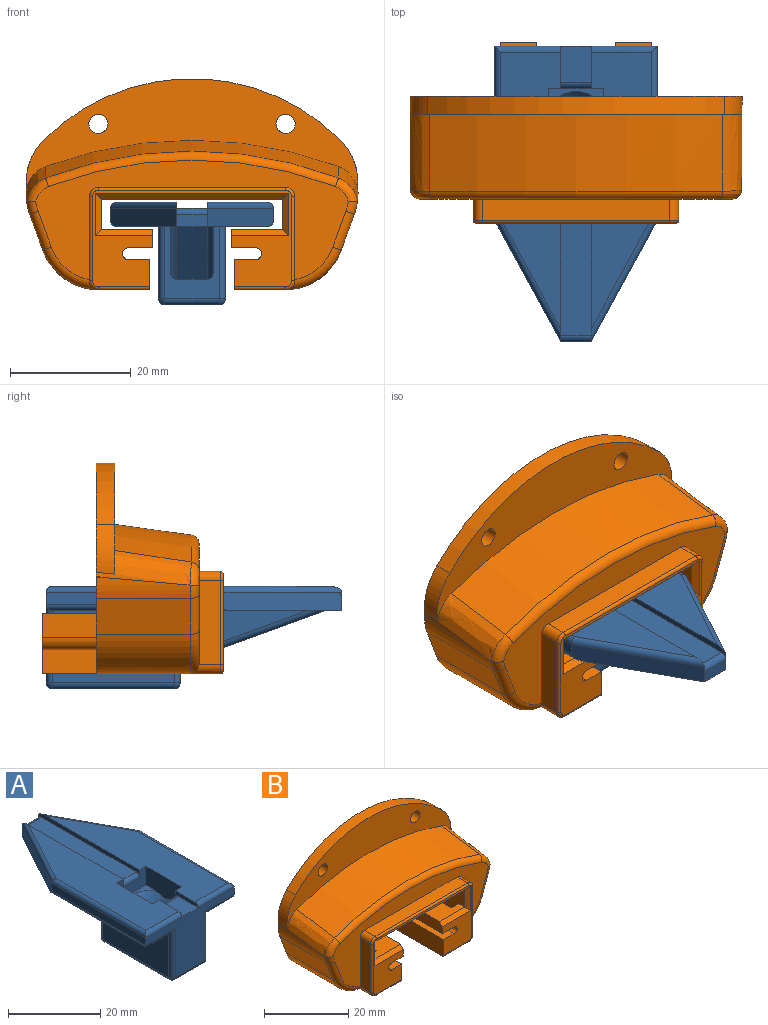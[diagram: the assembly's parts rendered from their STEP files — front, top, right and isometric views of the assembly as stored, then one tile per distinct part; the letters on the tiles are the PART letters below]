
ASSEMBLY  parts=2 mates=1
PART A: 58 faces, bbox 27.2x49.2x17.2 mm
  f0: plane 5x2mm, normal (0,1,0), area 10mm2, adj f2,f3,f15,f57
  f1: plane 20.2x12mm, normal (-1,0,0), area 242.4mm2, adj f15,f37,f43,f46
  f2: plane 20.2x11mm, normal (0.88,0.48,0), area 68.6mm2, adj f0,f9,f15,f16,f31,f49
  f3: plane 20.2x11mm, normal (-0.88,0.48,0), area 68.6mm2, adj f0,f13,f15,f17,f33,f52
  f4: plane 45.91x10mm, normal (0,0,1), area 345.3mm2, adj f12,f13,f19,f20,f22,f50,f51,f52
  f5: plane 45.91x10mm, normal (0,0,1), area 345.3mm2, adj f8,f9,f19,f20,f21,f47,f48,f49
  f6: plane 20.2x9mm, normal (0,0,-1), area 131.5mm2, adj f38,f39,f43,f44,f54
  f7: plane 9x3.32mm, normal (0,0,1), area 11.7mm2, adj f20,f21,f22,f25
  f8: plane 7x2mm, normal (-1,0,0), area 7mm2, adj f5,f10,f19,f47,f55
  f9: plane 31x2mm, normal (-1,0,0), area 31mm2, adj f2,f5,f11,f20,f49,f56,f57
  f10: plane 6x5mm, normal (0,0,1), area 30mm2, adj f8,f12,f18,f55
  f11: plane 29x5mm, normal (0,0,1), area 145mm2, adj f9,f13,f56,f57
  f12: plane 7x2mm, normal (1,0,0), area 7mm2, adj f4,f10,f19,f50,f55
  f13: plane 31x2mm, normal (1,0,0), area 31mm2, adj f3,f4,f11,f20,f52,f56,f57
  f14: plane 20.2x12mm, normal (1,0,0), area 242.4mm2, adj f15,f34,f39,f40
  f15: plane 48x25mm, normal (0,0,-1), area 616.6mm2, adj f0,f1,f2,f3,f14,f26,f27,f28
  f16: plane 28.8x2mm, normal (1,0,0), area 57.6mm2, adj f2,f18,f31,f48
  f17: plane 28.8x2mm, normal (-1,0,0), area 57.6mm2, adj f3,f18,f33,f51
  f18: plane 27x15mm, normal (0,-1,0), area 171mm2, adj f10,f16,f17,f32,f34,f35,f37,f38
  f19: plane 9x5mm, normal (0,1,0), area 35mm2, adj f4,f5,f8,f12,f21,f22,f23,f55
  f20: plane 9x5mm, normal (0,-1,0), area 35mm2, adj f4,f5,f7,f9,f13,f21,f22,f56
  f21: plane 11x5.51mm, normal (-1,0,0), area 56.4mm2, adj f5,f7,f19,f20,f23,f25
  f22: plane 11x5.5mm, normal (1,0,0), area 56.4mm2, adj f4,f7,f19,f20,f23,f25
  f23: plane 9x3.32mm, normal (0,0,1), area 11.7mm2, adj f19,f21,f22,f25
  f24: cylinder r=3mm len=9mm, axis (0,0,1), area 169.6mm2, adj f25,f54
  f25: cone r=3mm half-angle=45deg, axis (0,0,1), area 66.9mm2, adj f7,f21,f22,f23,f24
  f26: plane 12.15x9.15mm, normal (0,1,0), area 47.2mm2, adj f15,f27,f28,f29,f30,f40,f44,f46
  f27: plane 21.12x7.69mm, normal (1,0,0), area 81.1mm2, adj f15,f26,f53
  f28: plane 24.04x8.75mm, normal (0,0.34,-0.94), area 127.9mm2, adj f15,f26,f30,f53
  f29: plane 21.12x7.69mm, normal (-1,0,0), area 81.1mm2, adj f15,f26,f30
  f30: cylinder r=1mm len=24.38mm, axis (0,-0.94,-0.34), area 38.3mm2, adj f15,f26,f28,f29
  f31: cylinder r=1mm len=30.64mm, axis (0,1,0), area 45.7mm2, adj f2,f15,f16,f32
  f32: cylinder r=1mm len=9mm, axis (-1,0,0), area 12.6mm2, adj f15,f18,f31,f34
  f33: cylinder r=1mm len=30.64mm, axis (0,-1,0), area 45.7mm2, adj f3,f15,f17,f35
  f34: cylinder r=1mm len=13mm, axis (0,0,-1), area 19.4mm2, adj f14,f18,f32,f36
  f35: cylinder r=1mm len=9mm, axis (1,0,0), area 12.6mm2, adj f15,f18,f33,f37
  f36: sphere r=1mm, area 1.6mm2, adj f34,f38,f39
  f37: cylinder r=1mm len=13mm, axis (0,0,1), area 19.4mm2, adj f1,f18,f35,f41
  f38: cylinder r=1mm len=9mm, axis (-1,0,0), area 14.1mm2, adj f6,f18,f36,f41
  f39: cylinder r=1mm len=20.2mm, axis (0,1,0), area 31.7mm2, adj f6,f14,f36,f42
  f40: cylinder r=1mm len=12mm, axis (0,0,-1), area 18.8mm2, adj f14,f15,f26,f42
  f41: sphere r=1mm, area 1.6mm2, adj f37,f38,f43
  f42: sphere r=1mm, area 1.6mm2, adj f39,f40,f44
  f43: cylinder r=1mm len=20.2mm, axis (0,-1,0), area 31.7mm2, adj f1,f6,f41,f45
  f44: cylinder r=1mm len=9mm, axis (-1,0,0), area 14.1mm2, adj f6,f26,f42,f45
  f45: sphere r=1mm, area 1.6mm2, adj f43,f44,f46
  f46: cylinder r=1mm len=12mm, axis (0,0,-1), area 18.8mm2, adj f1,f15,f26,f45
  f47: cylinder r=1mm len=11mm, axis (1,0,0), area 16.7mm2, adj f5,f8,f18,f48
  f48: cylinder r=1mm len=28.8mm, axis (0,1,0), area 44.5mm2, adj f5,f16,f47,f49
  f49: cylinder r=1mm len=20.68mm, axis (0.48,-0.88,0), area 34.9mm2, adj f2,f5,f9,f48
  f50: cylinder r=1mm len=11mm, axis (1,0,0), area 16.7mm2, adj f4,f12,f18,f51
  f51: cylinder r=1mm len=28.8mm, axis (0,1,0), area 44.5mm2, adj f4,f17,f50,f52
  f52: cylinder r=1mm len=20.68mm, axis (-0.48,-0.88,0), area 34.9mm2, adj f3,f4,f13,f51
  f53: cylinder r=1mm len=24.38mm, axis (0,0.94,0.34), area 38.3mm2, adj f15,f26,f27,f28
  f54: torus R=4mm, axis (0,0,1), area 33.2mm2, adj f6,f24
  f55: cylinder r=1mm len=5mm, axis (-1,0,0), area 7.9mm2, adj f8,f10,f12,f19
  f56: cylinder r=1mm len=5mm, axis (1,0,0), area 7.9mm2, adj f9,f11,f13,f20
  f57: cylinder r=1mm len=5mm, axis (-1,0,0), area 7.9mm2, adj f0,f9,f11,f13
PART B: 137 faces, bbox 55.1x88.3x35.9 mm
  f0: plane 29x8.5mm, normal (0,0,1), area 179mm2, adj f30,f36,f41,f53,f123,f135
  f1: plane 9.5x9.04mm, normal (0,1,0), area 53.1mm2, adj f6,f11,f12,f28,f71,f90,f104
  f2: plane 55.01x35.01mm, normal (0,1,0), area 376.1mm2, adj f5,f8,f11,f21,f22,f24,f25,f26
  f3: plane 35x10mm, normal (0,1,0), area 125mm2, adj f6,f12,f14,f28,f29,f30,f79,f82
  f4: plane 0.84x0.5mm, normal (0,0,-1), area 0.4mm2, adj f8,f10,f74,f135
  f5: cylinder r=3.5mm len=18.5mm, axis (0,-1,0), area 41.8mm2, adj f2,f7,f52,f71,f83,f136
  f6: plane 14.5x2.5mm, normal (0,0,-1), area 36.2mm2, adj f1,f3,f12,f28
  f7: plane 0.84x0.5mm, normal (0,0,-1), area 0.4mm2, adj f5,f9,f83,f136
  f8: cylinder r=3.5mm len=18.5mm, axis (0,-1,0), area 41.8mm2, adj f2,f4,f53,f69,f74,f135
  f9: plane 5x0.5mm, normal (-1,0,0), area 2.5mm2, adj f7,f71,f83,f136
  f10: plane 5x0.5mm, normal (1,0,0), area 2.5mm2, adj f4,f69,f74,f135
  f11: plane 14.5x5.96mm, normal (-0.94,0,0.34), area 77.1mm2, adj f1,f2,f19,f90,f91,f103,f104,f105
  f12: plane 14.5x10mm, normal (1,0,0), area 131mm2, adj f1,f3,f6,f14,f19,f103,f104,f105
  f13: plane 9.47x5.86mm, normal (0,1,0), area 31.5mm2, adj f14,f18,f78,f79,f88,f92,f98,f100
  f14: plane 35x14.5mm, normal (0,0,1), area 465.5mm2, adj f3,f12,f13,f15,f19,f70,f79,f85
  f15: plane 14x3.13mm, normal (0,1,0), area 36.1mm2, adj f14,f16,f96,f99
  f16: cone r=65.52mm half-angle=8deg, axis (0,1,0), area 199.6mm2, adj f15,f85,f96,f99
  f17: plane 9.5x9.04mm, normal (0,1,0), area 53.1mm2, adj f30,f69,f78,f79,f82,f89,f101
  f18: cone r=65.52mm half-angle=8deg, axis (0,1,0), area 116.4mm2, adj f13,f85,f92,f98
  f19: plane 9.47x5.86mm, normal (0,1,0), area 31.5mm2, adj f11,f12,f14,f20,f91,f93,f95,f103
  f20: cone r=65.52mm half-angle=8deg, axis (0,1,0), area 116.4mm2, adj f19,f85,f93,f95
  f21: plane 1.31x0.2mm, normal (-1,0,0), area 0.1mm2, adj f2,f63,f67
  f22: cylinder r=34.71mm len=49.17mm, axis (0,1,0), area 163.9mm2, adj f2,f60,f61,f62
  f23: plane 51.81x19.84mm, normal (0,-1,0), area 348mm2, adj f56,f57,f58,f107,f108,f110,f111,f112
  f24: plane 1.31x0.2mm, normal (1,0,0), area 0.1mm2, adj f2,f66,f68
  f25: plane 15.5x5.96mm, normal (-0.94,0,-0.34), area 98.3mm2, adj f2,f63,f64,f113
  f26: plane 15.5x5.96mm, normal (0.94,0,-0.34), area 98.3mm2, adj f2,f65,f66,f108
  f27: plane 29.5x8.32mm, normal (0,0,-1), area 179.6mm2, adj f2,f36,f45,f48,f64,f124
  f28: plane 20x12.5mm, normal (-1,0,0), area 162.5mm2, adj f1,f3,f6,f29,f40,f71,f120,f136
  f29: plane 30x20mm, normal (0,0,-1), area 600mm2, adj f3,f28,f30,f121
  f30: plane 20x12.5mm, normal (1,0,0), area 162.5mm2, adj f0,f3,f17,f29,f69,f82,f122,f135
  f31: plane 10x6mm, normal (0,1,0), area 29.1mm2, adj f34,f37,f38,f39,f40,f46,f47,f49
  f32: cylinder r=1.59mm len=3.18mm, axis (0,-1,0), area 29.9mm2, adj f2,f60
  f33: cylinder r=1.59mm len=3.18mm, axis (0,-1,0), area 29.9mm2, adj f2,f60
  f34: plane 29.5x8.32mm, normal (0,0,-1), area 179.6mm2, adj f2,f31,f46,f49,f65,f130
  f35: plane 33x16mm, normal (0,-1,0), area 169mm2, adj f37,f38,f39,f41,f42,f43,f44,f45
  f36: plane 10x6mm, normal (0,1,0), area 29.1mm2, adj f0,f27,f41,f42,f43,f44,f45,f48
  f37: cylinder r=1mm len=30mm, axis (0,-1,0), area 94.2mm2, adj f31,f35,f38,f47
  f38: plane 30x4mm, normal (0,0,-1), area 120mm2, adj f31,f35,f37,f39
  f39: plane 30x3mm, normal (-1,0,0), area 89.5mm2, adj f31,f35,f38,f40,f119
  f40: plane 29x8.5mm, normal (0,0,1), area 179mm2, adj f28,f31,f39,f52,f119,f136
  f41: plane 30x3mm, normal (1,0,0), area 89.5mm2, adj f0,f35,f36,f42,f123
  f42: plane 30x4mm, normal (0,0,-1), area 120mm2, adj f35,f36,f41,f43
  f43: cylinder r=1mm len=30mm, axis (0,-1,0), area 94.2mm2, adj f35,f36,f42,f44
  f44: plane 30x3.5mm, normal (0,0,1), area 105mm2, adj f35,f36,f43,f45
  f45: plane 30x5mm, normal (1,0,0), area 149.9mm2, adj f27,f35,f36,f44,f124
  f46: plane 30x5mm, normal (-1,0,0), area 149.9mm2, adj f31,f34,f35,f47,f130
  f47: plane 30x3.5mm, normal (0,0,1), area 105mm2, adj f31,f35,f37,f46
  f48: plane 9x4mm, normal (-1,0,0), area 36mm2, adj f2,f27,f36,f55
  f49: plane 9x4mm, normal (1,0,0), area 36mm2, adj f2,f31,f34,f50
  f50: plane 9x2.5mm, normal (0,0,-1), area 22.5mm2, adj f2,f31,f49,f51
  f51: cylinder r=2mm len=9mm, axis (0,1,0), area 28.3mm2, adj f2,f31,f50,f52
  f52: plane 27x6.87mm, normal (1,0,0), area 159.7mm2, adj f2,f5,f31,f40,f51,f136
  f53: plane 27x6.87mm, normal (-1,0,0), area 159.7mm2, adj f0,f2,f8,f36,f54,f135
  f54: cylinder r=2mm len=9mm, axis (0,1,0), area 28.3mm2, adj f2,f36,f53,f55
  f55: plane 9x2.5mm, normal (0,0,-1), area 22.5mm2, adj f2,f36,f48,f54
  f56: plane 31x3.5mm, normal (0,0,1), area 108.5mm2, adj f23,f117,f118,f129
  f57: plane 14x3.51mm, normal (1,0,0), area 49mm2, adj f23,f106,f107,f117,f133
  f58: plane 14x3.51mm, normal (-1,0,0), area 49mm2, adj f23,f109,f111,f118,f127
  f59: cone r=68mm half-angle=8deg, axis (0,1,0), area 635.7mm2, adj f60,f67,f68,f114
  f60: plane 55x18.45mm, normal (0,-1,0), area 423.8mm2, adj f22,f32,f33,f59,f61,f62,f67,f68
  f61: cylinder r=10mm len=8.24mm, axis (0,1,0), area 26.7mm2, adj f2,f22,f60,f68
  f62: cylinder r=10mm len=8.24mm, axis (0,1,0), area 26.7mm2, adj f2,f22,f60,f67
  f63: cylinder r=10mm len=15.5mm, axis (0,1,0), area 45.6mm2, adj f2,f21,f25,f67,f115
  f64: cylinder r=10mm len=20.5mm, axis (0,-1,0), area 190.1mm2, adj f2,f25,f27,f109,f111,f125
  f65: cylinder r=10mm len=20.5mm, axis (0,1,0), area 190.1mm2, adj f2,f26,f34,f106,f107,f132
  f66: cylinder r=10mm len=15.5mm, axis (0,1,0), area 45.6mm2, adj f2,f24,f26,f68,f110
  f67: bspline ~88.18x17.81mm, area 73.5mm2, adj f2,f21,f59,f60,f62,f63,f115,f116
  f68: bspline ~88.18x17.81mm, area 73.5mm2, adj f2,f24,f59,f60,f61,f66,f110,f112
  f69: plane 18.5x4.82mm, normal (0,0,1), area 87.6mm2, adj f2,f8,f10,f17,f30,f74,f89,f135
  f70: plane 14x3.13mm, normal (0,1,0), area 36.1mm2, adj f14,f84,f94,f97
  f71: plane 18.5x4.82mm, normal (0,0,1), area 87.6mm2, adj f1,f2,f5,f9,f28,f83,f90,f136
  f72: cylinder r=32.21mm len=24.62mm, axis (0,1,0), area 12.6mm2, adj f2,f80,f81,f85
  f73: cylinder r=32.21mm len=3.49mm, axis (0,1,0), area 2.3mm2, adj f2,f80,f85,f86
  f74: plane 5x4mm, normal (0,1,0), area 5.3mm2, adj f4,f8,f10,f69
  f75: plane 1.31x0.2mm, normal (1,0,0), area 0.1mm2, adj f2,f88,f92
  f76: cylinder r=32.21mm len=3.49mm, axis (0,1,0), area 2.3mm2, adj f2,f81,f85,f87
  f77: plane 1.31x0.2mm, normal (-1,0,0), area 0.1mm2, adj f2,f91,f93
  f78: plane 14.5x5.96mm, normal (0.94,0,0.34), area 77.1mm2, adj f2,f13,f17,f88,f89,f100,f101,f102
  f79: plane 14.5x10mm, normal (-1,0,0), area 131mm2, adj f3,f13,f14,f17,f82,f100,f101,f102
  f80: cylinder r=4.09mm len=7.91mm, axis (0,-1,0), area 7.1mm2, adj f2,f72,f73,f85
  f81: cylinder r=4.09mm len=7.91mm, axis (0,-1,0), area 7.1mm2, adj f2,f72,f76,f85
  f82: plane 14.5x2.5mm, normal (0,0,-1), area 36.3mm2, adj f3,f17,f30,f79
  f83: plane 5x4mm, normal (0,1,0), area 5.3mm2, adj f5,f7,f9,f71
  f84: cone r=65.52mm half-angle=8deg, axis (0,1,0), area 199.6mm2, adj f70,f85,f94,f97
  f85: plane 50.1x15.91mm, normal (0,1,0), area 337.6mm2, adj f14,f16,f18,f20,f72,f73,f76,f80
  f86: cylinder r=7.5mm len=6.34mm, axis (0,1,0), area 3.5mm2, adj f2,f73,f85,f93
  f87: cylinder r=7.5mm len=6.34mm, axis (0,1,0), area 3.5mm2, adj f2,f76,f85,f92
  f88: cylinder r=7.5mm len=14.5mm, axis (0,1,0), area 29.9mm2, adj f2,f13,f75,f78,f92
  f89: cylinder r=7.5mm len=14.5mm, axis (0,-1,0), area 132.7mm2, adj f2,f17,f69,f78
  f90: cylinder r=7.5mm len=14.5mm, axis (0,1,0), area 132.7mm2, adj f1,f2,f11,f71
  f91: cylinder r=7.5mm len=14.5mm, axis (0,1,0), area 29.9mm2, adj f2,f11,f19,f77,f93
  f92: bspline ~87.83x15.46mm, area 38.5mm2, adj f2,f13,f18,f75,f85,f87,f88
  f93: bspline ~87.83x15.46mm, area 38.5mm2, adj f2,f19,f20,f77,f85,f86,f91
  f94: plane 14.01x3.54mm, normal (-1,0,0), area 35.4mm2, adj f14,f70,f84,f85
  f95: plane 14.01x3.31mm, normal (1,0,0), area 32.1mm2, adj f14,f19,f20,f85
  f96: plane 14x5.1mm, normal (-1,0,0), area 57.6mm2, adj f14,f15,f16,f85
  f97: plane 14x5.1mm, normal (1,0,0), area 57.6mm2, adj f14,f70,f84,f85
  f98: plane 14.01x3.31mm, normal (-1,0,0), area 32.1mm2, adj f13,f14,f18,f85
  f99: plane 14.01x3.54mm, normal (1,0,0), area 35.4mm2, adj f14,f15,f16,f85
  f100: plane 14x6.9mm, normal (0,0,1), area 96.7mm2, adj f13,f78,f79,f102
  f101: plane 14x6.54mm, normal (0,0,-1), area 91.5mm2, adj f17,f78,f79,f102
  f102: plane 6.9x1mm, normal (0,1,0), area 6.7mm2, adj f78,f79,f100,f101
  f103: plane 14x6.9mm, normal (0,0,1), area 96.7mm2, adj f11,f12,f19,f105
  f104: plane 14x6.54mm, normal (0,0,-1), area 91.5mm2, adj f1,f11,f12,f105
  f105: plane 6.9x1mm, normal (0,1,0), area 6.7mm2, adj f11,f12,f103,f104
  f106: cylinder r=1.5mm len=5mm, axis (0,1,0), area 9.9mm2, adj f57,f65,f107,f134
  f107: torus R=8.5mm, axis (0,-1,0), area 24.4mm2, adj f23,f57,f65,f106,f108
  f108: cylinder r=1.5mm len=6.47mm, axis (-0.34,0,-0.94), area 14.9mm2, adj f23,f26,f107,f110
  f109: cylinder r=1.5mm len=5mm, axis (0,-1,0), area 9.9mm2, adj f58,f64,f111,f126
  f110: torus R=8.5mm, axis (0,-1,0), area 4.8mm2, adj f23,f66,f68,f108,f112
  f111: torus R=8.5mm, axis (0,-1,0), area 24.4mm2, adj f23,f58,f64,f109,f113
  f112: bspline ~4.88x3.89mm, area 9.9mm2, adj f23,f68,f110,f114
  f113: cylinder r=1.5mm len=6.47mm, axis (-0.34,0,0.94), area 14.9mm2, adj f23,f25,f111,f115
  f114: torus R=66.7mm, axis (0,-1,0), area 105.6mm2, adj f23,f59,f112,f116
  f115: torus R=8.5mm, axis (0,-1,0), area 4.8mm2, adj f23,f63,f67,f113,f116
  f116: bspline ~4.88x3.89mm, area 9.9mm2, adj f23,f67,f114,f115
  f117: cylinder r=1.5mm len=3.5mm, axis (0,-1,0), area 8.2mm2, adj f23,f56,f57,f131
  f118: cylinder r=1.5mm len=3.5mm, axis (0,1,0), area 8.2mm2, adj f23,f56,f58,f128
  f119: plane 9.5x1mm, normal (0,-0.71,0.71), area 12.7mm2, adj f35,f39,f40,f120
  f120: plane 7x1mm, normal (-0.71,-0.71,0), area 8.5mm2, adj f28,f35,f119,f121
  f121: plane 32x1mm, normal (0,-0.71,-0.71), area 43.8mm2, adj f29,f35,f120,f122
  f122: plane 7x1mm, normal (0.71,-0.71,0), area 8.5mm2, adj f30,f35,f121,f123
  f123: plane 9.5x1mm, normal (0,-0.71,0.71), area 12.7mm2, adj f0,f35,f41,f122
  f124: cylinder r=0.5mm len=8.32mm, axis (-1,0,0), area 6.5mm2, adj f27,f35,f45,f125
  f125: torus R=9.5mm, axis (0,-1,0), area 0.2mm2, adj f35,f64,f124,f126
  f126: torus R=1mm, axis (0,-1,0), area 1.6mm2, adj f35,f109,f125,f127
  f127: cylinder r=0.5mm len=14mm, axis (0,0,-1), area 11mm2, adj f35,f58,f126,f128
  f128: torus R=1mm, axis (0,-1,0), area 1.6mm2, adj f35,f118,f127,f129
  f129: cylinder r=0.5mm len=31mm, axis (-1,0,0), area 24.3mm2, adj f35,f56,f128,f131
  f130: cylinder r=0.5mm len=8.32mm, axis (-1,0,0), area 6.5mm2, adj f34,f35,f46,f132
  f131: torus R=1mm, axis (0,-1,0), area 1.6mm2, adj f35,f117,f129,f133
  f132: torus R=9.5mm, axis (0,-1,0), area 0.2mm2, adj f35,f65,f130,f134
  f133: cylinder r=0.5mm len=14mm, axis (0,0,1), area 11mm2, adj f35,f57,f131,f134
  f134: torus R=1mm, axis (0,-1,0), area 1.6mm2, adj f35,f106,f132,f133
  f135: plane 7.5x2.5mm, normal (0,1,0), area 13.9mm2, adj f0,f4,f8,f10,f30,f53,f69
  f136: plane 7.5x2.5mm, normal (0,1,0), area 13.9mm2, adj f5,f7,f9,f28,f40,f52,f71
PLACE A rot(axis=(0,0,1),180deg) t=(2.5,-19.66,-8.59)mm
PLACE B t=(-27.5,30,-6.09)mm
MATE slider B.f3 <-> A.f18  axis (0,1,0) through (0,21,6.41)mm
